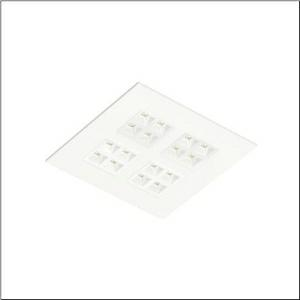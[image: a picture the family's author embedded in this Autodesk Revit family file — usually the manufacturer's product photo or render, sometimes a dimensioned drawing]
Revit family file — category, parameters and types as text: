
# Revit family: silica_31_square_51my6nms44wa
name_source: partatom
category: Lighting Fixtures
units: mm (PartAtom-declared; Revit-internal decimal feet)

## family parameters
Cut with Voids When Loaded = No
Host = Face
Light Source = No
Part Type = Normal
Room Calculation Point = No
Round Connector Dimension = Use Diameter
Shared = No

## types (1)
- --- (1 x LED, 6970 lm, 39 W, 4000K)
    Apparent Load = 39 VA
    CIE Flux Codes = 81 99 100 100 100
    Color Rendering = 80
    Color Temperature = 4000K
    Default Elevation = 1800 mm
    Description = Silica 31 Square, office luminaire, primary light control with lens, of PMMA, primary anti-glare with reflector, of PC, white, light emission: direct distribution, primary light characteristic: symmetric, installation type: lay-in mounting, LED, rated luminous flux: 4.560lm, luminous efficacy: 186lm/W, light colour: 840, colour temperature: 4000K, control gear: ON/OFF Multilumen, with terminal, 3-pole, mains connection: 220..240V, AC, 50/60Hz, rated input power: 24.5W, luminaire housing, of sheet steel, coated, traffic white (RAL 9016), module: M600, length: 595mm, width: 595mm, height: 43mm, protection rating (complete): IP20, insulation class (complete): insulation class II (safety insulation), certification: CE, impact resistance: IK03, permissible operating ambient temperature: -20..+35°C, standard: EN 50419, packaging unit: 1 piece
    Height = 0 mm  [stored 0 ft]
    Lamp = 1 x LED
    Lamp Light Flux = 6970 lm
    Lamp Power = 39 W
    Lamp count = 1
    Length = 595 mm
    Luminous efficacy = 179 lm/W
    Manufacturer = Siteco
    ModVariant = No
    Model = 51MY6NMS44WA
    Mounting Place = Ceiling
    Mounting Type = Recessed
    Number of Poles = 1
    OnlyDefault = Yes
    Power Factor = 1
    Product Name = Silica 31 Square
    Product group = office luminaire | ceiling recessed
    ProductGroupID = 400
    Protection Class = Protection class II
    Protection Degree = IP 20
    RLX_Detail_Level = 1
    RLX_Emergency_Light_Flux = 0 lm
    RLX_Emergency_Type = 0
    RLX_Emergency_Type_DB = No
    RlxData = <blob elided: 28577 chars, md5=db92354e>
    Socket = socket
    Standby Power = 0 W
    System Light Flux = 6970 lm
    System Power = 39 W
    Type Comments = factory setting: luminous flux: 100 % | (ON | ON | ON | ON) | 1100 mA
    Type Image = l_1313651.jpg
    URL = http://relux.com
    VarID = @adj_043065
    Voltage = 0 V
    Weight = 0.00 kg
    Width = 595 mm

note: [stored X ft] marks values corroborated as IEEE doubles in the binary element streams (Revit-internal decimal feet)

## geometry (parser evidence)
native form markers: Blend x4, Sweep x9
no freeform markers — native parametric forms only
